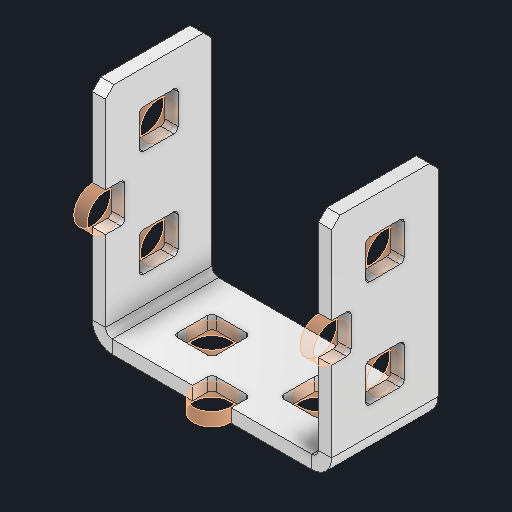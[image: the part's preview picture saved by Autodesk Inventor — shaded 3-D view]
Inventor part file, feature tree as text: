
AUTODESK INVENTOR PART (.ipt)
format: ipt  version: 2025 (Build 290162000, 162)  size: 361,984 bytes
history: native  units: in
note: dims shown in document units (in); Inventor stores cm internally (conversion verified against a paired STEP export)
features: other x173, sketch x2, sheet_metal_op x1
ambient origin geometry x8: Origin, YZ Plane, XZ Plane, XY Plane, X Axis, Y Axis, Z Axis, Center Point
bodies: Solid1 (feature_tree)
feature tree (176):
  other  "Alu C 2x2x2x1.ipt"
  other  "Solid1::Alu C 2x2x2x1.ipt"
  other  "TaggingFeature1"
  sketch  "Sketch1"  dims[d0=0.3937in]
  sketch  "Sketch2"  dims[d1=0.0625in]
  sheet_metal_op  "Body Pattern Sketch"
  other  "Arc Length"
  other  "Diagonal Plane"
  other  "Srf1"
  other  "Srf2"
  other  "Srf3"
  other  "Srf4"
  other  "Srf5"
  other  "Srf6"
  other  "Srf7"
  other  "Srf8"
  other  "Srf9"
  other  "Srf10"
  other  "Srf11"
  other  "Srf12"
  other  "Srf13"
  other  "Srf14"
  other  "Srf15"
  other  "Srf16"
  other  "Srf17"
  other  "Srf18"
  other  "Srf19"
  other  "Srf20"
  other  "Srf21"
  other  "Srf22"
  other  "Srf23"
  other  "Srf24"
  other  "Srf25"
  other  "Srf26"
  other  "Srf27"
  other  "Srf28"
  other  "Srf29"
  other  "Srf30"
  other  "Srf31"
  other  "Srf32"
  other  "Srf33"
  other  "Srf34"
  other  "Srf35"
  other  "Srf36"
  other  "Srf37"
  other  "Srf38"
  other  "Srf39"
  other  "Srf40"
  other  "Srf41"
  other  "Srf42"
  other  "Srf43"
  other  "Srf44"
  other  "Srf45"
  other  "Srf46"
  other  "Srf47"
  other  "Srf48"
  other  "Srf49"
  other  "Srf50"
  other  "Srf51"
  other  "Srf52"
  other  "Srf53"
  other  "Srf54"
  other  "Srf55"
  other  "Srf56"
  other  "Srf57"
  other  "Srf58"
  other  "Srf59"
  other  "Srf60"
  other  "Srf61"
  other  "Srf62"
  other  "Srf63"
  other  "Srf64"
  other  "Srf65"
  other  "Srf66"
  other  "Srf67"
  other  "Srf68"
  other  "Srf69"
  other  "Srf70"
  other  "Srf71"
  other  "Srf72"
  other  "Srf73"
  other  "Srf74"
  other  "Srf75"
  other  "Srf76"
  other  "Srf77"
  other  "Srf78"
  other  "Srf79"
  other  "Srf80"
  other  "Srf81"
  other  "Srf82"
  other  "Srf83"
  other  "Srf84"
  other  "Srf91::Derived"
  other  "Srf92::Derived"
  other  "Srf786::Derived"
  other  "Srf889::Derived"
  other  "Srf890::Derived"
  other  "Srf891::Derived"
  other  "Srf892::Derived"
  other  "Srf893::Derived"
  other  "Srf894::Derived"
  other  "Srf895::Derived"
  other  "Srf896::Derived"
  other  "Srf996::Derived"
  other  "Srf997::Derived"
  other  "Srf998::Derived"
  other  "Srf999::Derived"
  other  "Srf1000::Derived"
  other  "Srf1255::Derived"
  other  "Srf1256::Derived"
  other  "Srf1257::Derived"
  other  "Srf1258::Derived"
  other  "Srf1259::Derived"
  other  "Srf1315::Derived"
  other  "Srf1316::Derived"
  other  "Srf1317::Derived"
  other  "Srf1325::Derived"
  other  "Srf1326::Derived"
  other  "Srf1327::Derived"
  other  "Srf1328::Derived"
  other  "Srf1329::Derived"
  other  "Srf1330::Derived"
  other  "Srf1331::Derived"
  other  "Srf1332::Derived"
  other  "Srf1338::Derived"
  other  "Srf1339::Derived"
  other  "Srf1340::Derived"
  other  "Srf1341::Derived"
  other  "Srf1342::Derived"
  other  "Srf1369::Derived"
  other  "Srf1370::Derived"
  other  "Srf1371::Derived"
  other  "Srf1372::Derived"
  other  "Srf1373::Derived"
  other  "Srf1374::Derived"
  other  "Srf1375::Derived"
  other  "Srf1376::Derived"
  other  "Srf1384::Derived"
  other  "Srf1385::Derived"
  other  "Srf1386::Derived"
  other  "Srf1387::Derived"
  other  "Srf1388::Derived"
  other  "Srf1389::Derived"
  other  "Srf1390::Derived"
  other  "Srf1391::Derived"
  other  "Srf1397::Derived"
  other  "Srf1398::Derived"
  other  "Srf1399::Derived"
  other  "Srf1400::Derived"
  other  "Srf1401::Derived"
  other  "Srf1428::Derived"
  other  "Srf1429::Derived"
  other  "Srf1430::Derived"
  other  "Srf1431::Derived"
  other  "Srf1432::Derived"
  other  "Srf1433::Derived"
  other  "Srf1434::Derived"
  other  "Srf1473::Derived"
  other  "Srf1474::Derived"
  other  "Srf1475::Derived"
  other  "Srf1476::Derived"
  other  "Srf1477::Derived"
  other  "Srf1478::Derived"
  other  "Srf1479::Derived"
  other  "Srf1480::Derived"
  other  "Srf1481::Derived"
  other  "Srf1482::Derived"
  other  "Srf1483::Derived"
  other  "Srf1484::Derived"
  other  "Srf1485::Derived"
  other  "Srf1486::Derived"
  other  "Srf1487::Derived"
  other  "Srf1488::Derived"
  other  "Srf1489::Derived"
  other  "Srf1490::Derived"
  other  "Srf1491::Derived"
